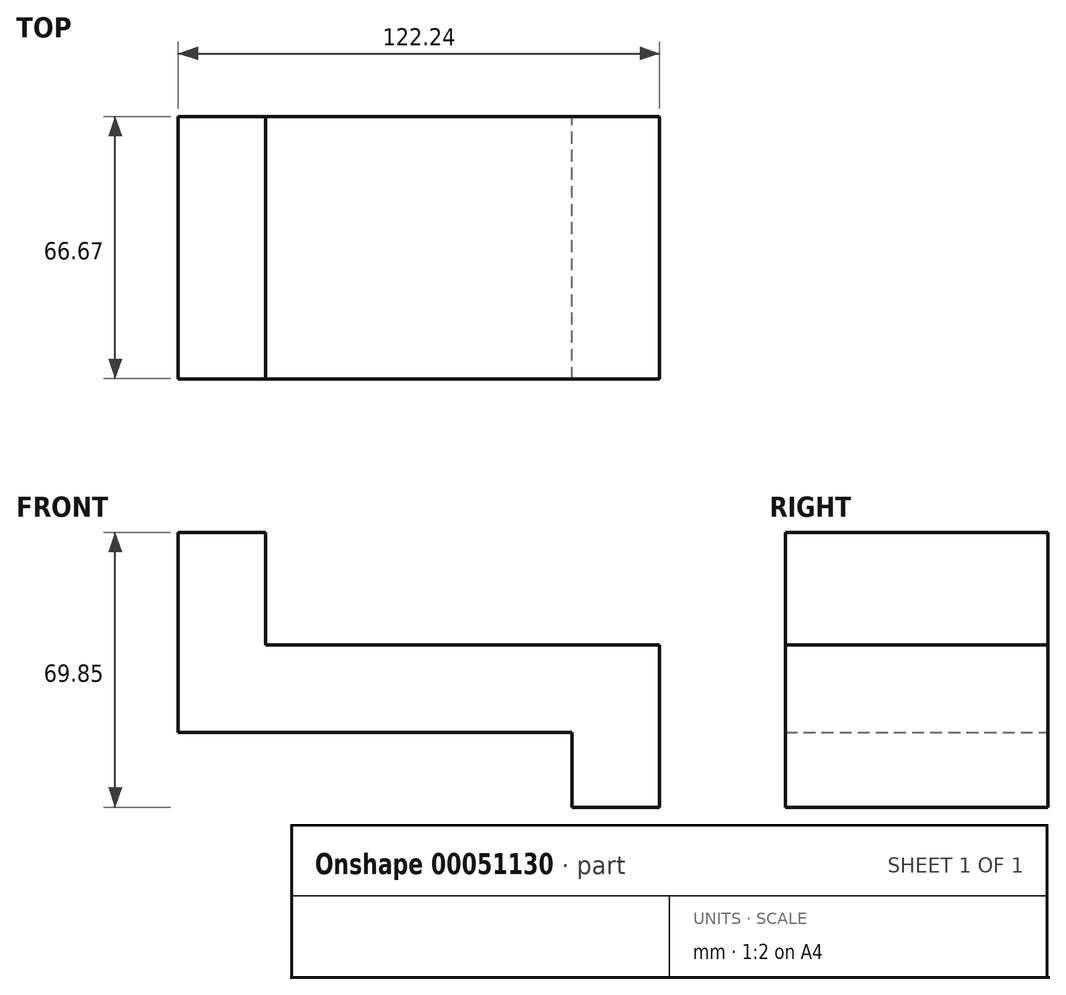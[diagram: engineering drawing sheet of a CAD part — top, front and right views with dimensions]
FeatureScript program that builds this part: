
annotation { "Feature Type Name" : "Feature", "Feature Type Description" : "" }
export const myFeature = defineFeature(function(context is Context, id is Id, definition is map)
    precondition{}
    {
        {
            var Q0;
            Q0=qCreatedBy(makeId("Front.planeOp"),FACE);
            var sketch = newSketch(context, id + "F0", { "sketchPlane" : qUnion([Q0])});
            skLineSegment(sketch, "E0", {"start": v(-61.62, 0) * mm, "end": v(38.4, 0) * mm});
            skLineSegment(sketch, "E1", {"start": v(-61.62, 0) * mm, "end": v(-61.62, 50.8) * mm});
            skLineSegment(sketch, "E2", {"start": v(-61.62, 50.8) * mm, "end": v(-39.4, 50.8) * mm});
            skLineSegment(sketch, "E3", {"start": v(-39.4, 50.8) * mm, "end": v(-39.4, 22.22) * mm});
            skLineSegment(sketch, "E4", {"start": v(-39.4, 22.22) * mm, "end": v(60.62, 22.23) * mm});
            skLineSegment(sketch, "E5", {"start": v(60.62, -19.05) * mm, "end": v(38.4, -19.05) * mm});
            skLineSegment(sketch, "E6", {"start": v(38.4, -19.05) * mm, "end": v(38.4, 0) * mm});
            skPoint(sketch, "E7.orphan", {"position": v(60.62, 0) * mm});
            skLineSegment(sketch, "E8", {"start": v(60.62, 22.23) * mm, "end": v(60.62, -19.05) * mm});
            skSolve(sketch);
        }
        {
            var Q0;
            Q0 = qSketchRegion(id + "F0", true);
            extrude(context, id + "F1", {"entities" : qUnion([Q0]), "depth" : 66.67 * mm});
        }
    });
